# Revit family: STH21920BR_30_40_STH21920PTO_30
name_source: partatom
category: Luminárias
units: mm (PartAtom-declared; Revit-internal decimal feet)

## family parameters
Compartilhado = Não
Corte com vazios quando carregada = Não
Cota do conector redondo = Utilizar diâmetro
Fonte luminosa = Sim
Hospedeiro = Forro
Manter orientação da anotação = Não
Número OmniClass = 23.80.70.11
Ponto de cálculo do ambiente = Não
Sempre na vertical = Sim
Tipo de parte = Normal
Título OmniClass = Luminaries for Internal Lighting

## types (3) — shared parameters
Altura = 0.06 m
Comprimento = 0.1 m
Cromado = Cromado
Dimerização = Não dimerizável
Fabricante = Stella
Filtro de cor = 16777215
Grau de proteção (IP) = IP20
IRC (Índice de reprodução de cores) = >80
Largura = 0.1 m
Modelo = Easy MR16 Evo
Potência = 5 W
Tensão Elétrica = 100V-240V
Troca de temperatura da cor de lâmpada com esmaecimento = <Nenhum>
URL = https://stella.com.br
Vidro = Vidro
Ângulo de Abertura = 34°
Ângulo de inclinação = 90.00°
zero-valued in all types: Elevação padrão

## per-type parameters (varying)
| type | Arquivo de rede fotométrica | Estrutura | Fluxo Luminoso | Luminoso | Referência | Temperatura da cor (K) |
| STH21920BR/30 - BRANCO - BIVOLT - 3000K - 340lm - 34° | STELLA - STH21920BR-30 - EASY MR16 EMBUTIDO RECUADO DIRECIONÁVEL.ies | Al - Branco | 340 lm | Luminoso - 3000K | STH21920BR/30 | 3000 K |
| STH21920BR/40 - BRANCO - BIVOLT - 4000K - 350lm - 34° | STELLA - STH21920BR-40 - EASY MR16 EMBUTIDO RECUADO DIRECIONÁVEL.ies | Al - Branco | 350 lm | Luminoso - 4000K | STH21920BR/40 | 4000 K |
| STH21920PTO/30 - PRETO - BIVOLT - 3000K - 330lm - 34° | STELLA - STH21920PTO-30 - EASY MR16 EMBUTIDO RECUADO DIRECIONÁVEL.ies | Al - Preto | 330 lm | Luminoso - 3000K | STH21920PTO/30 | 3000 K |
